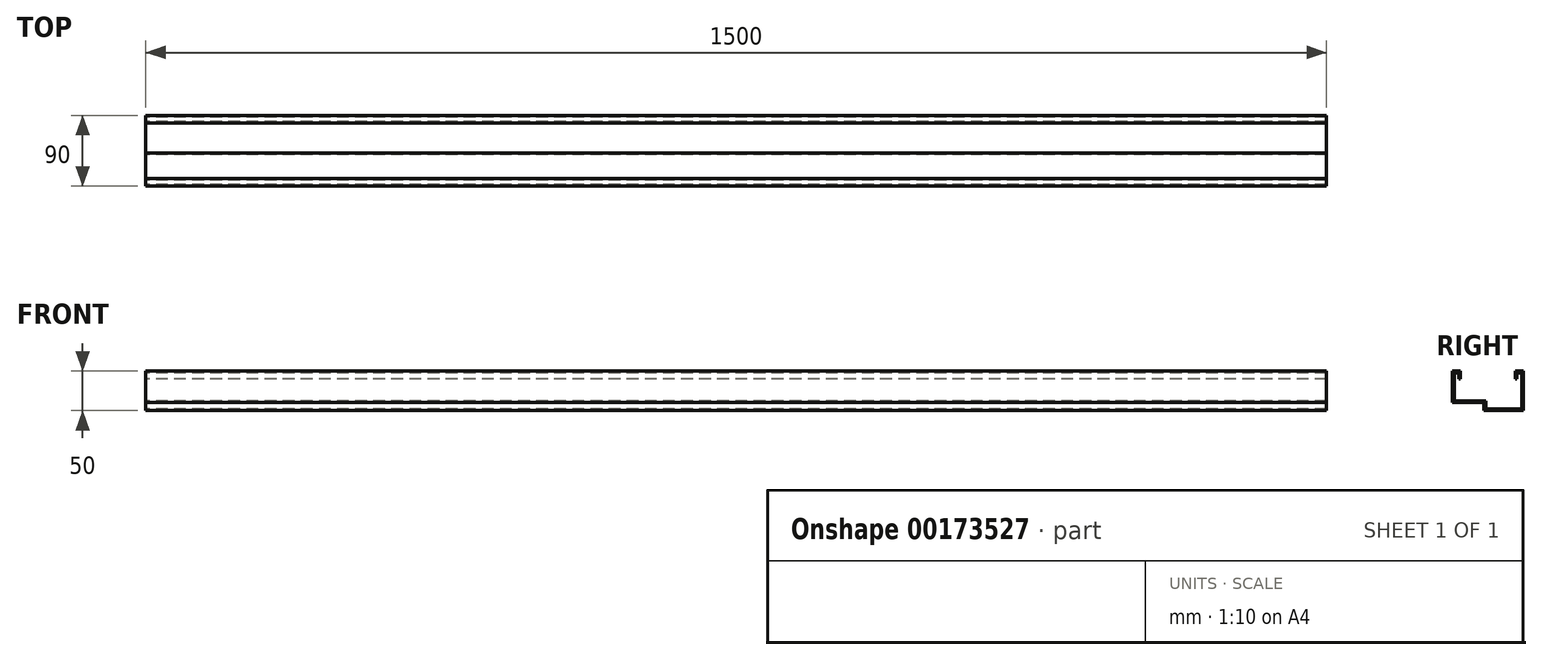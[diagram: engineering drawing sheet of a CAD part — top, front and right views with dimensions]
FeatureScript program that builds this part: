
annotation { "Feature Type Name" : "Feature", "Feature Type Description" : "" }
export const myFeature = defineFeature(function(context is Context, id is Id, definition is map)
    precondition{}
    {
        {
            var Q0;
            Q0=qCreatedBy(makeId("Top.planeOp"),FACE);
            var sketch = newSketch(context, id + "F0", { "sketchPlane" : qUnion([Q0])});
            skLineSegment(sketch, "E0", {"start": v(0, 0) * mm, "end": v(0, -10) * mm});
            skLineSegment(sketch, "E1", {"start": v(0, -10) * mm, "end": v(40, -10) * mm});
            skLineSegment(sketch, "E2", {"start": v(40, -10) * mm, "end": v(40, 30) * mm});
            skLineSegment(sketch, "E3", {"start": v(40, 30) * mm, "end": v(50, 30) * mm});
            skLineSegment(sketch, "E4", {"start": v(50, 30) * mm, "end": v(50, 80) * mm});
            skLineSegment(sketch, "E5", {"start": v(50, 80) * mm, "end": v(0, 80) * mm});
            skLineSegment(sketch, "E6", {"start": v(0, 80) * mm, "end": v(0, 70) * mm});
            skLineSegment(sketch, "E7", {"start": v(0, 0) * mm, "end": v(10, 0) * mm});
            skLineSegment(sketch, "E8", {"start": v(0, 70) * mm, "end": v(10, 70) * mm});
            skLineSegment(sketch, "E9.0", {"start": v(2, 72) * mm, "end": v(10, 72) * mm});
            skLineSegment(sketch, "E10.0", {"start": v(2, 78) * mm, "end": v(2, 72) * mm});
            skLineSegment(sketch, "E11", {"start": v(10, 70) * mm, "end": v(10, 72) * mm});
            skLineSegment(sketch, "E12.0", {"start": v(48, 78) * mm, "end": v(2, 78) * mm});
            skLineSegment(sketch, "E13.0", {"start": v(48, 32) * mm, "end": v(48, 78) * mm});
            skLineSegment(sketch, "E13.1", {"start": v(38, 32) * mm, "end": v(48, 32) * mm});
            skLineSegment(sketch, "E13.2", {"start": v(2, -2) * mm, "end": v(10, -2) * mm});
            skLineSegment(sketch, "E13.3", {"start": v(2, -2) * mm, "end": v(2, -8) * mm});
            skLineSegment(sketch, "E13.4", {"start": v(2, -8) * mm, "end": v(38, -8) * mm});
            skLineSegment(sketch, "E13.5", {"start": v(38, -8) * mm, "end": v(38, 32) * mm});
            skLineSegment(sketch, "E14", {"start": v(10, 0) * mm, "end": v(10, -2) * mm});
            skSolve(sketch);
        }
        {
            var Q0;
            Q0=makeQuery(id+"F0.imprint","IMPRINT",FACE,{"disambiguationData":[TD([[makeQuery(id+"F0.imprint","IMPRINT",EDGE,{"derivedFrom":sQuery(id+"F0.wireOp",EDGE,"E0")}),1.0]])]});
            var Q1;
            Q1=sQuery(id+"F0.wireOp",EDGE,"E2");
            var Q2;
            Q2=sQuery(id+"F0.wireOp",EDGE,"E3");
            var Q3;
            Q3=sQuery(id+"F0.wireOp",EDGE,"E4");
            var Q4;
            Q4=sQuery(id+"F0.wireOp",EDGE,"E5");
            var Q5;
            Q5=sQuery(id+"F0.wireOp",EDGE,"E6");
            var Q6;
            Q6=sQuery(id+"F0.wireOp",EDGE,"E7");
            var Q7;
            Q7=sQuery(id+"F0.wireOp",EDGE,"E8");
            var Q8;
            Q8=sQuery(id+"F0.wireOp",EDGE,"E1");
            var Q9;
            Q9=sQuery(id+"F0.wireOp",EDGE,"E0");
            extrude(context, id + "F1", {"entities" : qUnion([Q0]), "surfaceEntities" : qUnion([Q1, Q2, Q3, Q4, Q5, Q6, Q7, Q8, Q9]), "depth" : 800 * mm});
        }
        {
            var Q0;
            Q0=makeQuery(id+"F1.opExtrude","SWEPT_BODY",BODY,{"disambiguationData":[OSD([sQuery(id+"F0.wireOp",EDGE,"E0"),sQuery(id+"F0.wireOp",EDGE,"E1"),sQuery(id+"F0.wireOp",EDGE,"E2"),sQuery(id+"F0.wireOp",EDGE,"E3"),sQuery(id+"F0.wireOp",EDGE,"E4"),sQuery(id+"F0.wireOp",EDGE,"E5"),sQuery(id+"F0.wireOp",EDGE,"E6"),sQuery(id+"F0.wireOp",EDGE,"E7"),sQuery(id+"F0.wireOp",EDGE,"E8"),sQuery(id+"F0.wireOp",EDGE,"E9.0"),sQuery(id+"F0.wireOp",EDGE,"E10.0"),sQuery(id+"F0.wireOp",EDGE,"E11"),sQuery(id+"F0.wireOp",EDGE,"E12.0"),sQuery(id+"F0.wireOp",EDGE,"E13.0"),sQuery(id+"F0.wireOp",EDGE,"E13.1"),sQuery(id+"F0.wireOp",EDGE,"E13.2"),sQuery(id+"F0.wireOp",EDGE,"E13.3"),sQuery(id+"F0.wireOp",EDGE,"E13.4"),sQuery(id+"F0.wireOp",EDGE,"E13.5"),sQuery(id+"F0.wireOp",EDGE,"E14")])]});
            var Q1;
            Q1=makeQuery(id+"F1.opExtrude","CAP_EDGE",EDGE,{"disambiguationData":[OSD([sQuery(id+"F0.wireOp",EDGE,"E4")])],"isStart":false});
            transform(context, id + "F2", {"entities" : qUnion([Q0]), "transformType" : TransformType.ROTATION, "transformAxis" : qUnion([Q1]), "angle" : 180 * degree, "makeCopy" : false});
        }
        {
            var Q0;
            Q0=makeQuery(id+"F1.opExtrude","SWEPT_BODY",BODY,{"disambiguationData":[OSD([sQuery(id+"F0.wireOp",EDGE,"E0"),sQuery(id+"F0.wireOp",EDGE,"E1"),sQuery(id+"F0.wireOp",EDGE,"E2"),sQuery(id+"F0.wireOp",EDGE,"E3"),sQuery(id+"F0.wireOp",EDGE,"E4"),sQuery(id+"F0.wireOp",EDGE,"E5"),sQuery(id+"F0.wireOp",EDGE,"E6"),sQuery(id+"F0.wireOp",EDGE,"E7"),sQuery(id+"F0.wireOp",EDGE,"E8"),sQuery(id+"F0.wireOp",EDGE,"E9.0"),sQuery(id+"F0.wireOp",EDGE,"E10.0"),sQuery(id+"F0.wireOp",EDGE,"E11"),sQuery(id+"F0.wireOp",EDGE,"E12.0"),sQuery(id+"F0.wireOp",EDGE,"E13.0"),sQuery(id+"F0.wireOp",EDGE,"E13.1"),sQuery(id+"F0.wireOp",EDGE,"E13.2"),sQuery(id+"F0.wireOp",EDGE,"E13.3"),sQuery(id+"F0.wireOp",EDGE,"E13.4"),sQuery(id+"F0.wireOp",EDGE,"E13.5"),sQuery(id+"F0.wireOp",EDGE,"E14")])]});
            var Q1;
            Q1=makeQuery(id+"F1.opExtrude","CAP_EDGE",EDGE,{"disambiguationData":[OSD([sQuery(id+"F0.wireOp",EDGE,"E4")])],"isStart":false});
            transform(context, id + "F3", {"entities" : qUnion([Q0]), "transformType" : TransformType.ROTATION, "transformAxis" : qUnion([Q1]), "angle" : 270 * degree, "makeCopy" : false});
        }
        {
            var Q0;
            Q0=makeQuery(id+"F1.opExtrude","SWEPT_BODY",BODY,{"disambiguationData":[OSD([sQuery(id+"F0.wireOp",EDGE,"E0"),sQuery(id+"F0.wireOp",EDGE,"E1"),sQuery(id+"F0.wireOp",EDGE,"E2"),sQuery(id+"F0.wireOp",EDGE,"E3"),sQuery(id+"F0.wireOp",EDGE,"E4"),sQuery(id+"F0.wireOp",EDGE,"E5"),sQuery(id+"F0.wireOp",EDGE,"E6"),sQuery(id+"F0.wireOp",EDGE,"E7"),sQuery(id+"F0.wireOp",EDGE,"E8"),sQuery(id+"F0.wireOp",EDGE,"E9.0"),sQuery(id+"F0.wireOp",EDGE,"E10.0"),sQuery(id+"F0.wireOp",EDGE,"E11"),sQuery(id+"F0.wireOp",EDGE,"E12.0"),sQuery(id+"F0.wireOp",EDGE,"E13.0"),sQuery(id+"F0.wireOp",EDGE,"E13.1"),sQuery(id+"F0.wireOp",EDGE,"E13.2"),sQuery(id+"F0.wireOp",EDGE,"E13.3"),sQuery(id+"F0.wireOp",EDGE,"E13.4"),sQuery(id+"F0.wireOp",EDGE,"E13.5"),sQuery(id+"F0.wireOp",EDGE,"E14")])]});
            var Q1;
            Q1=qCreatedBy(makeId("Right.planeOp"),FACE);
            mirror(context, id + "F4", {"operationType" : NewBodyOperationType.ADD, "entities" : qUnion([Q0]), "mirrorPlane" : qUnion([Q1])});
        }
    });
